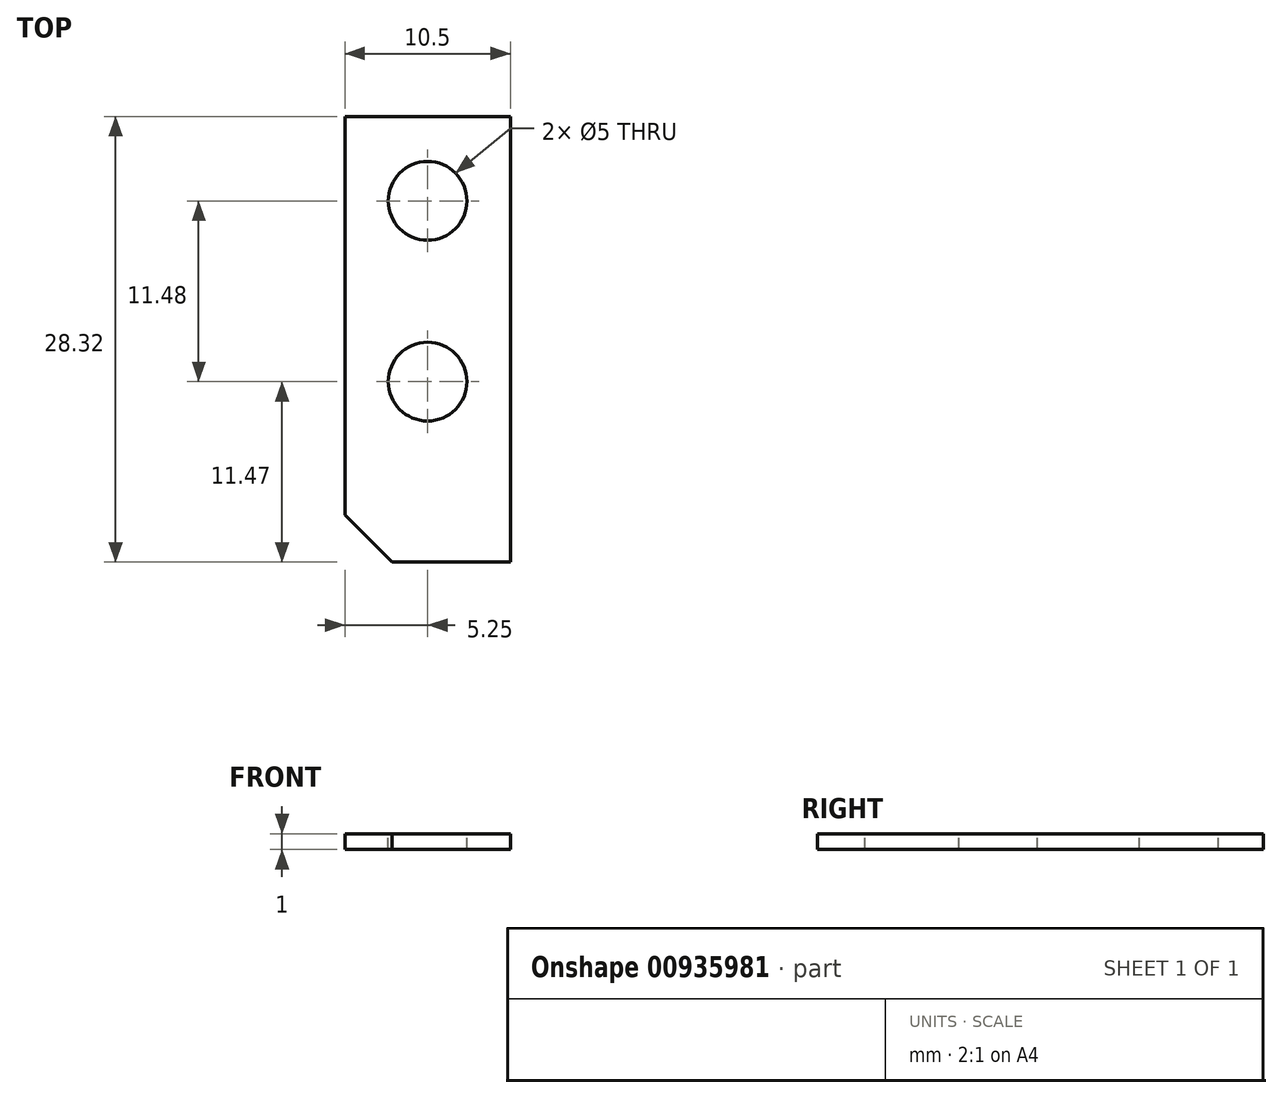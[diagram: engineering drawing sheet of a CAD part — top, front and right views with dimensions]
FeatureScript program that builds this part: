
annotation { "Feature Type Name" : "Feature", "Feature Type Description" : "" }
export const myFeature = defineFeature(function(context is Context, id is Id, definition is map)
    precondition{}
    {
        {
            var Q0;
            Q0=qCreatedBy(makeId("Top.planeOp"),FACE);
            var sketch = newSketch(context, id + "F0", { "sketchPlane" : qUnion([Q0])});
            skLineSegment(sketch, "E0.bottom", {"start": v(5.25, -14.16) * mm, "end": v(-5.25, -14.16) * mm});
            skLineSegment(sketch, "E0.top", {"start": v(5.25, 14.16) * mm, "end": v(-5.25, 14.16) * mm});
            skLineSegment(sketch, "E0.left", {"start": v(5.25, -14.16) * mm, "end": v(5.25, 14.16) * mm});
            skLineSegment(sketch, "E0.right", {"start": v(-5.25, -14.16) * mm, "end": v(-5.25, 14.16) * mm});
            skPoint(sketch, "E0.middle", {"position": v(0, 0) * mm});
            skSolve(sketch);
        }
        {
            var Q0;
            Q0 = qSketchRegion(id + "F0", true);
            extrude(context, id + "F1", {"entities" : qUnion([Q0]), "depth" : 1 * mm, "offsetDistance" : 25 * mm});
        }
        {
            var Q0;
            Q0=makeQuery(id+"F1.opExtrude","CAP_FACE",FACE,{"disambiguationData":[OSD([sQuery(id+"F0.wireOp",EDGE,"E0.bottom"),sQuery(id+"F0.wireOp",EDGE,"E0.top"),sQuery(id+"F0.wireOp",EDGE,"E0.left"),sQuery(id+"F0.wireOp",EDGE,"E0.right")])],"isStart":false});
            var sketch = newSketch(context, id + "F2", { "sketchPlane" : qUnion([Q0])});
            skLineSegment(sketch, "E1", {"start": v(0, -14.16) * mm, "end": v(0, -5.2) * mm});
            skCircle(sketch, "E2", {"center": v(0, -2.7) * mm, "radius": 2.5 * mm});
            skLineSegment(sketch, "E3", {"start": v(0, -0.2) * mm, "end": v(0, 6.29) * mm});
            skCircle(sketch, "E4", {"center": v(0, 8.79) * mm, "radius": 2.5 * mm});
            skSolve(sketch);
        }
        {
            var Q0;
            Q0=makeQuery(id+"F2.imprint","IMPRINT",FACE,{"disambiguationData":[TD([[makeQuery(id+"F2.imprint","IMPRINT",EDGE,{"derivedFrom":sQuery(id+"F2.wireOp",EDGE,"E4")}),1.0]])]});
            var Q1;
            {var subQ0=sQuery(id+"F2.wireOp",EDGE,"E2");var subQ1=makeQuery(id+"F2.imprint","IMPRINT",VERTEX,{"disambiguationData":[OD(0.0)],"derivedFrom":subQ0});Q1=makeQuery(id+"F2.imprint","IMPRINT",FACE,{"disambiguationData":[TD([[makeQuery(id+"F2.imprint","IMPRINT",EDGE,{"disambiguationData":[TD([[subQ1,1.0]])],"derivedFrom":subQ0}),1.0]])]});}
            extrude(context, id + "F3", {"entities" : qUnion([Q0, Q1]), "operationType" : NewBodyOperationType.REMOVE, "oppositeDirection" : true, "depth" : 1.5 * mm, "offsetDistance" : 25 * mm});
        }
        {
            var Q0;
            Q0=makeQuery(id+"F1.opExtrude","SWEPT_EDGE",EDGE,{"disambiguationData":[OSD([sQuery(id+"F0.wireOp",EDGE,"E0.bottom"),sQuery(id+"F0.wireOp",EDGE,"E0.right")])]});
            chamfer(context, id + "F4", {"entities" : qUnion([Q0]), "width" : 3 * mm, "tangentPropagation" : true});
        }
    });
